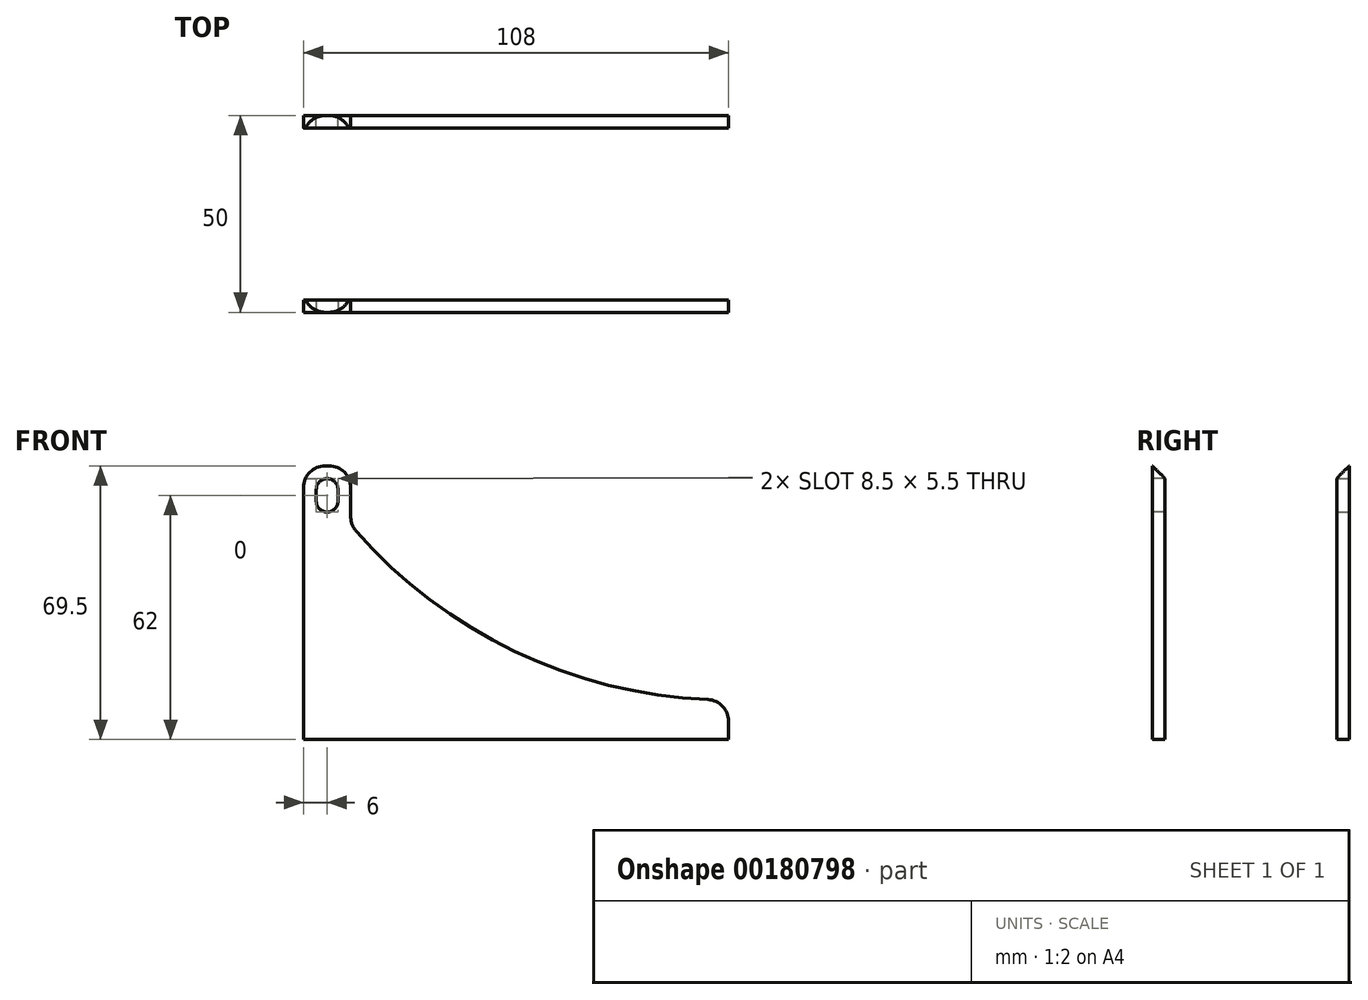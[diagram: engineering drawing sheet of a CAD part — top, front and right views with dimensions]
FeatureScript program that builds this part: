
annotation { "Feature Type Name" : "Feature", "Feature Type Description" : "" }
export const myFeature = defineFeature(function(context is Context, id is Id, definition is map)
    precondition{}
    {
        {
            var Q0;
            Q0=qCreatedBy(makeId("Front.planeOp"),FACE);
            var sketch = newSketch(context, id + "F0", { "sketchPlane" : qUnion([Q0])});
            skLineSegment(sketch, "E0.top", {"start": v(12, 69.5) * mm, "end": v(0, 69.5) * mm});
            skArc(sketch, "E1", {"start": v(8.75, 63.5) * mm, "mid": v(6, 66.25) * mm, "end": v(3.25, 63.5) * mm});
            skLineSegment(sketch, "E2", {"start": v(0, 69.5) * mm, "end": v(0, 0) * mm});
            skLineSegment(sketch, "E3", {"start": v(0, 0) * mm, "end": v(108, 0) * mm});
            skArc(sketch, "E4", {"start": v(12, 69.5) * mm, "mid": v(71.26, 50.3) * mm, "end": v(108, 0) * mm, "construction": true});
            skLineSegment(sketch, "E5", {"start": v(108, 0) * mm, "end": v(108, 10) * mm});
            skLineSegment(sketch, "E6", {"start": v(108, 10) * mm, "end": v(0, 10) * mm, "construction": true});
            skLineSegment(sketch, "E7", {"start": v(12, 69.5) * mm, "end": v(12, 54.5) * mm});
            skArc(sketch, "E8", {"start": v(12, 54.5) * mm, "mid": v(55.1, 21.67) * mm, "end": v(108, 10) * mm});
            skArc(sketch, "E9", {"start": v(3.25, 60.5) * mm, "mid": v(6, 57.75) * mm, "end": v(8.75, 60.5) * mm});
            skLineSegment(sketch, "E10", {"start": v(3.25, 60.5) * mm, "end": v(3.25, 63.5) * mm});
            skLineSegment(sketch, "E11", {"start": v(8.75, 63.5) * mm, "end": v(8.75, 60.5) * mm});
            skSolve(sketch);
        }
        {
            var Q0;
            Q0=makeQuery(id+"F0.imprint","IMPRINT",FACE,{"disambiguationData":[TD([[makeQuery(id+"F0.imprint","IMPRINT",EDGE,{"derivedFrom":sQuery(id+"F0.wireOp",EDGE,"E0.top")}),1.0]])]});
            var Q1;
            Q1=makeQuery(id+"F0.imprint","IMPRINT",FACE,{"disambiguationData":[TD([[makeQuery(id+"F0.imprint","IMPRINT",EDGE,{"derivedFrom":sQuery(id+"F0.wireOp",EDGE,"owF4AePb-eyHH-hYSw-2OuU-yM0CS4dCG3sK")}),-1.0]])]});
            extrude(context, id + "F1", {"entities" : qUnion([Q0, Q1]), "depth" : 3.17 * mm, "offsetDistance" : 25 * mm});
        }
        {
            var Q0;
            Q0=makeQuery(id+"F1.opExtrude","SWEPT_EDGE",EDGE,{"disambiguationData":[OSD([sQuery(id+"F0.wireOp",EDGE,"E0.top"),sQuery(id+"F0.wireOp",EDGE,"E2")])]});
            var Q1;
            Q1=makeQuery(id+"F1.opExtrude","SWEPT_EDGE",EDGE,{"disambiguationData":[OSD([sQuery(id+"F0.wireOp",EDGE,"E0.top"),sQuery(id+"F0.wireOp",EDGE,"jek2T68t-vuzY-tIHw-5Fmq-EDm088HEf1P8")])]});
            var Q2;
            Q2=makeQuery(id+"F1.opExtrude","SWEPT_EDGE",EDGE,{"disambiguationData":[OSD([sQuery(id+"F0.wireOp",EDGE,"E7"),sQuery(id+"F0.wireOp",EDGE,"E8")])]});
            var Q3;
            Q3=makeQuery(id+"F1.opExtrude","SWEPT_EDGE",EDGE,{"disambiguationData":[OSD([sQuery(id+"F0.wireOp",EDGE,"E5"),sQuery(id+"F0.wireOp",EDGE,"E8")])]});
            fillet(context, id + "F2", {"entities" : qUnion([Q0, Q1, Q2, Q3]), "radius" : 5.5 * mm, "tangentPropagation" : true, "allowEdgeOverflow" : false});
        }
        {
            var Q0;
            Q0=qCreatedBy(makeId("Right.planeOp"),FACE);
            var sketch = newSketch(context, id + "F3", { "sketchPlane" : qUnion([Q0])});
            skLineSegment(sketch, "E12.0", {"start": v(-3.18, 69.5) * mm, "end": v(0, 69.5) * mm});
            skLineSegment(sketch, "E13.0", {"start": v(-3.18, 66.33) * mm, "end": v(-3.18, 69.5) * mm});
            skLineSegment(sketch, "E14", {"start": v(-3.17, 66.33) * mm, "end": v(0, 69.5) * mm});
            skSolve(sketch);
        }
        {
            var Q0;
            Q0 = qSketchRegion(id + "F3", true);
            extrude(context, id + "F4", {"entities" : qUnion([Q0]), "operationType" : NewBodyOperationType.REMOVE, "endBound" : BoundingType.THROUGH_ALL, "oppositeDirection" : true, "depth" : 25 * mm, "hasSecondDirection" : true, "secondDirectionBound" : SecondDirectionBoundingType.THROUGH_ALL, "secondDirectionOppositeDirection" : false, "secondDirectionDepth" : 25 * mm});
        }
        {
            var Q0;
            Q0=qCreatedBy(makeId("Front.planeOp"),FACE);
            cPlane(context, id + "F5", {"entities" : qUnion([Q0]), "cplaneType" : CPlaneType.OFFSET, "offset" : 25 * mm, "width" : 150 * mm, "height" : 150 * mm});
        }
        {
            var Q0;
            Q0=makeQuery(id+"F1.opExtrude","SWEPT_BODY",BODY,{"disambiguationData":[OSD([sQuery(id+"F0.wireOp",EDGE,"E0.top"),sQuery(id+"F0.wireOp",EDGE,"E1"),sQuery(id+"F0.wireOp",EDGE,"E2"),sQuery(id+"F0.wireOp",EDGE,"E3"),sQuery(id+"F0.wireOp",EDGE,"E5"),sQuery(id+"F0.wireOp",EDGE,"E7"),sQuery(id+"F0.wireOp",EDGE,"E8")])]});
            var Q1;
            Q1=qCreatedBy(id+"F5.planeOp",FACE);
            mirror(context, id + "F6", {"entities" : qUnion([Q0]), "mirrorPlane" : qUnion([Q1])});
        }
    });
